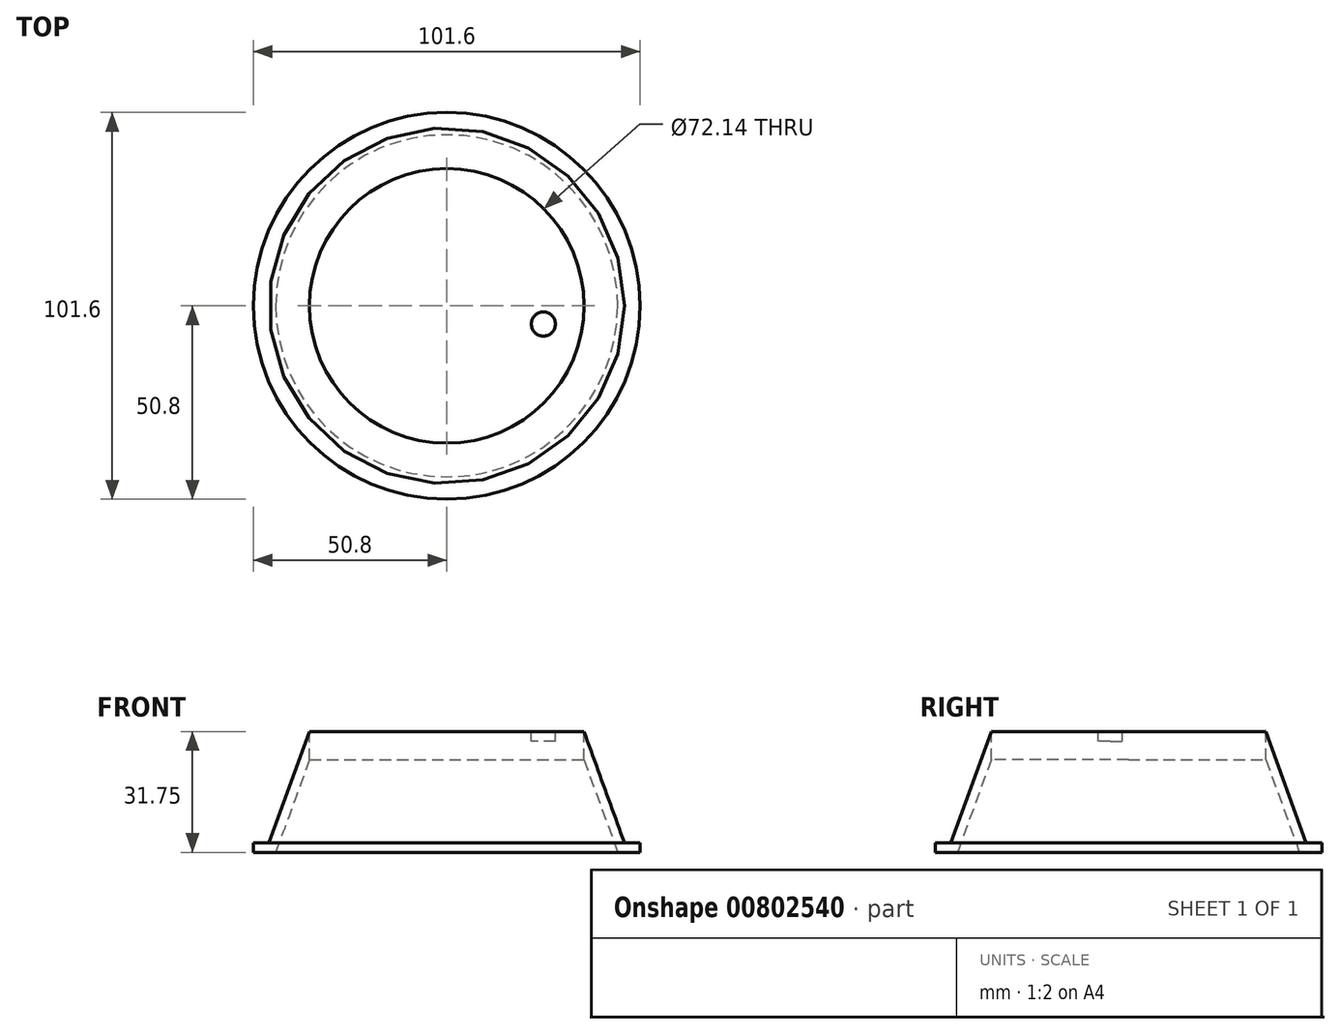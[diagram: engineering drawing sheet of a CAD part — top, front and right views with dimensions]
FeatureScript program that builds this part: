
annotation { "Feature Type Name" : "Feature", "Feature Type Description" : "" }
export const myFeature = defineFeature(function(context is Context, id is Id, definition is map)
    precondition{}
    {
        {
            var Q0;
            Q0=qCreatedBy(makeId("Front.planeOp"),FACE);
            var sketch = newSketch(context, id + "F0", { "sketchPlane" : qUnion([Q0])});
            skLineSegment(sketch, "E0", {"start": v(0, 130.85) * mm, "end": v(47.63, 0) * mm});
            skPoint(sketch, "E1.end.orphan", {"position": v(92.82, 0) * mm});
            skLineSegment(sketch, "E2", {"start": v(0, 0) * mm, "end": v(47.63, 0) * mm});
            skLineSegment(sketch, "E3", {"start": v(0, 130.85) * mm, "end": v(0, 0) * mm});
            skLineSegment(sketch, "E4", {"start": v(36.07, 31.75) * mm, "end": v(0, 31.75) * mm});
            skSolve(sketch);
        }
        {
            var Q0;
            {var subQ0=sQuery(id+"F0.wireOp",EDGE,"E2");Q0=makeQuery(id+"F0.imprint","IMPRINT",FACE,{"disambiguationData":[TD([[makeQuery(id+"F0.imprint","IMPRINT",EDGE,{"derivedFrom":subQ0}),1.0]])]});}
            var Q1;
            Q1=sQuery(id+"F0.wireOp",EDGE,"E3");
            revolve(context, id + "F1", {"surfaceOperationType" : NewSurfaceOperationType.NEW, "entities" : qUnion([Q0]), "axis" : qUnion([Q1]), "revolveType" : RevolveType.FULL});
        }
        {
            var Q0;
            Q0=makeQuery(id+"F1.opRevolve","SWEPT_FACE",FACE,{"disambiguationData":[OSD([sQuery(id+"F0.wireOp",EDGE,"E2")])]});
            shell(context, id + "F2", {"entities" : qUnion([Q0]), "thickness" : 2.54 * mm});
        }
        {
            var Q0;
            Q0=makeQuery(id+"F1.opRevolve","SWEPT_FACE",FACE,{"disambiguationData":[OSD([sQuery(id+"F0.wireOp",EDGE,"E2")])]});
            var sketch = newSketch(context, id + "F3", { "sketchPlane" : qUnion([Q0])});
            skCircle(sketch, "E5.0", {"center": v(0, 0) * mm, "radius": 47.63 * mm});
            skCircle(sketch, "E6", {"center": v(0, 0) * mm, "radius": 50.8 * mm});
            skSolve(sketch);
        }
        {
            var Q0;
            Q0=qCreatedBy(makeId("Right.planeOp"),FACE);
            var sketch = newSketch(context, id + "F4", { "sketchPlane" : qUnion([Q0])});
            skLineSegment(sketch, "E7.0", {"start": v(50.8, 0) * mm, "end": v(47.63, 0) * mm});
            skLineSegment(sketch, "E8", {"start": v(50.8, 0) * mm, "end": v(50.8, 2.54) * mm});
            skLineSegment(sketch, "E9", {"start": v(50.8, 2.54) * mm, "end": v(46.7, 2.54) * mm});
            skLineSegment(sketch, "E10", {"start": v(46.7, 2.54) * mm, "end": v(47.63, 0) * mm});
            skLineSegment(sketch, "E11.trimOffspring", {"start": v(-47.63, 0) * mm, "end": v(-50.8, 0) * mm});
            skSolve(sketch);
        }
        {
            var Q0;
            Q0=makeQuery(id+"F4.imprint","IMPRINT",FACE,{"disambiguationData":[TD([[makeQuery(id+"F4.imprint","IMPRINT",EDGE,{"derivedFrom":sQuery(id+"F4.wireOp",EDGE,"E7.0")}),-1.0]])]});
            var Q1;
            Q1=sQuery(id+"F3.wireOp",EDGE,"E5.0");
            revolve(context, id + "F5", {"operationType" : NewBodyOperationType.ADD, "surfaceOperationType" : NewSurfaceOperationType.NEW, "entities" : qUnion([Q0]), "axis" : qUnion([Q1]), "revolveType" : RevolveType.FULL});
        }
        {
            var Q0;
            Q0=makeQuery(id+"F1.opRevolve","SWEPT_FACE",FACE,{"disambiguationData":[OSD([sQuery(id+"F0.wireOp",EDGE,"E4")])]});
            var sketch = newSketch(context, id + "F6", { "sketchPlane" : qUnion([Q0])});
            skLineSegment(sketch, "E12.0", {"start": v(36.07, 0) * mm, "end": v(0, 0) * mm, "construction": true});
            skCircle(sketch, "E13", {"center": v(25.4, 4.76) * mm, "radius": 3.18 * mm});
            skCircle(sketch, "E14.MirrorC", {"center": v(25.4, -4.76) * mm, "radius": 3.18 * mm});
            skSolve(sketch);
        }
        {
            var Q0;
            Q0=makeQuery(id+"F6.imprint","IMPRINT",FACE,{"disambiguationData":[TD([[makeQuery(id+"F6.imprint","IMPRINT",EDGE,{"derivedFrom":sQuery(id+"F6.wireOp",EDGE,"E13")}),1.0]])]});
            var Q1;
            Q1=makeQuery(id+"F6.imprint","IMPRINT",FACE,{"disambiguationData":[TD([[makeQuery(id+"F6.imprint","IMPRINT",EDGE,{"derivedFrom":sQuery(id+"F6.wireOp",EDGE,"E14.MirrorC")}),-1.0]])]});
            extrude(context, id + "F7", {"entities" : qUnion([Q0, Q1]), "operationType" : NewBodyOperationType.REMOVE, "oppositeDirection" : true, "depth" : 25.4 * mm, "offsetDistance" : 25.4 * mm});
        }
    });
